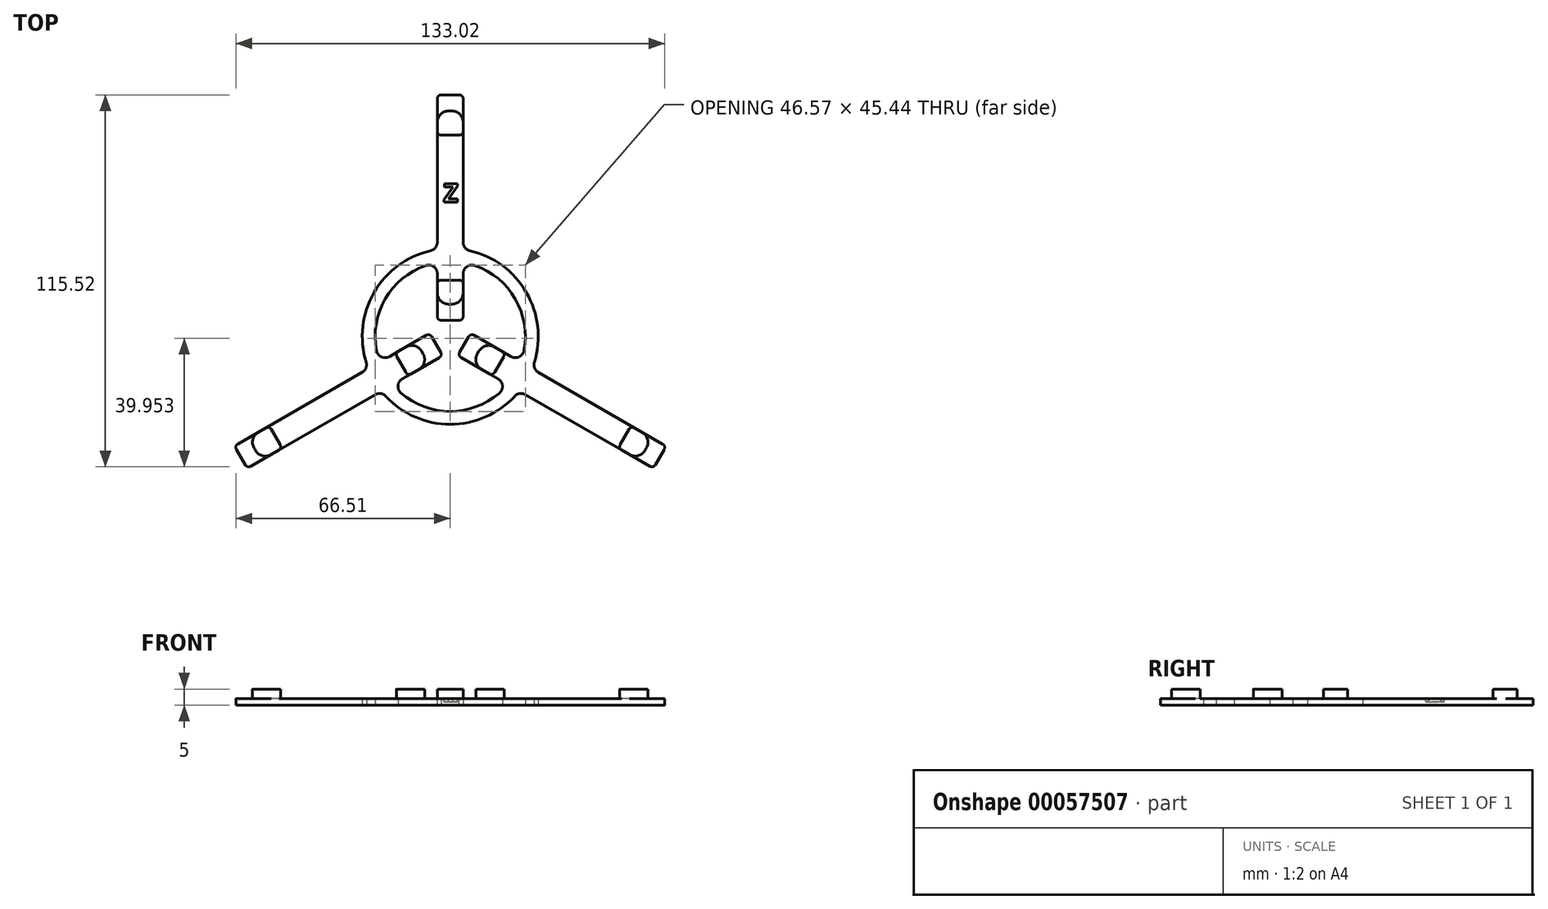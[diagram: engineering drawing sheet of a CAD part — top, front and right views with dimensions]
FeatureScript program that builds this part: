
annotation { "Feature Type Name" : "Feature", "Feature Type Description" : "" }
export const myFeature = defineFeature(function(context is Context, id is Id, definition is map)
    precondition{}
    {
        {
            var Q0;
            Q0=qCreatedBy(makeId("Top.planeOp"),FACE);
            var sketch = newSketch(context, id + "F0", { "sketchPlane" : qUnion([Q0])});
            skLineSegment(sketch, "E0", {"start": v(0, 0) * mm, "end": v(0, 85) * mm, "construction": true});
            skLineSegment(sketch, "E1", {"start": v(0, 0) * mm, "end": v(-73.61, -42.5) * mm, "construction": true});
            skLineSegment(sketch, "E2", {"start": v(0, 0) * mm, "end": v(73.61, -42.5) * mm, "construction": true});
            skLineSegment(sketch, "E3.rect.bottom", {"start": v(4, 5) * mm, "end": v(-4, 5) * mm});
            skLineSegment(sketch, "E3.rect.top", {"start": v(4, 75) * mm, "end": v(-4, 75) * mm});
            skLineSegment(sketch, "E3.rect.left", {"start": v(4, 5) * mm, "end": v(4, 75) * mm});
            skLineSegment(sketch, "E3.rect.right", {"start": v(-4, 5) * mm, "end": v(-4, 75) * mm});
            skPoint(sketch, "E3.rect.middle", {"position": v(0, 40) * mm});
            skLineSegment(sketch, "E4.rect.bottom", {"start": v(4, 10) * mm, "end": v(-4, 10) * mm});
            skLineSegment(sketch, "E4.rect.top", {"start": v(4, 17.5) * mm, "end": v(-4, 17.5) * mm});
            skLineSegment(sketch, "E4.rect.left", {"start": v(4, 10) * mm, "end": v(4, 17.5) * mm, "construction": true});
            skLineSegment(sketch, "E4.rect.right", {"start": v(-4, 10) * mm, "end": v(-4, 17.5) * mm, "construction": true});
            skPoint(sketch, "E4.rect.middle", {"position": v(0, 13.75) * mm});
            skLineSegment(sketch, "E5.rect.bottom", {"start": v(4, 70) * mm, "end": v(-4, 70) * mm});
            skLineSegment(sketch, "E5.rect.top", {"start": v(4, 62.5) * mm, "end": v(-4, 62.5) * mm});
            skLineSegment(sketch, "E5.rect.left", {"start": v(4, 70) * mm, "end": v(4, 62.5) * mm, "construction": true});
            skLineSegment(sketch, "E5.rect.right", {"start": v(-4, 70) * mm, "end": v(-4, 62.5) * mm, "construction": true});
            skPoint(sketch, "E5.rect.middle", {"position": v(0, 66.25) * mm});
            skPoint(sketch, "E6.1.0", {"position": v(-57.37, -33.12) * mm});
            skLineSegment(sketch, "E6.1.1", {"start": v(-6.33, 0.96) * mm, "end": v(-66.95, -34.04) * mm});
            skLineSegment(sketch, "E6.1.2", {"start": v(-2.33, -5.96) * mm, "end": v(-62.95, -40.96) * mm});
            skPoint(sketch, "E6.1.3", {"position": v(-11.9, -6.88) * mm});
            skPoint(sketch, "E6.1.4", {"position": v(-34.64, -20) * mm});
            skLineSegment(sketch, "E6.1.5", {"start": v(-58.62, -38.46) * mm, "end": v(-52.13, -34.71) * mm, "construction": true});
            skLineSegment(sketch, "E6.1.6", {"start": v(-6.33, 0.96) * mm, "end": v(-2.33, -5.96) * mm});
            skLineSegment(sketch, "E6.1.7", {"start": v(-66.95, -34.04) * mm, "end": v(-62.95, -40.96) * mm});
            skLineSegment(sketch, "E6.1.8", {"start": v(-62.62, -31.54) * mm, "end": v(-56.13, -27.79) * mm, "construction": true});
            skLineSegment(sketch, "E6.1.9", {"start": v(-56.13, -27.79) * mm, "end": v(-52.13, -34.71) * mm});
            skLineSegment(sketch, "E6.1.10", {"start": v(-10.66, -1.54) * mm, "end": v(-6.66, -8.46) * mm});
            skLineSegment(sketch, "E6.1.11", {"start": v(-17.16, -5.29) * mm, "end": v(-13.16, -12.21) * mm});
            skLineSegment(sketch, "E6.1.12", {"start": v(-10.66, -1.54) * mm, "end": v(-17.16, -5.29) * mm, "construction": true});
            skLineSegment(sketch, "E6.1.13", {"start": v(-62.62, -31.54) * mm, "end": v(-58.62, -38.46) * mm});
            skLineSegment(sketch, "E6.1.14", {"start": v(-6.66, -8.46) * mm, "end": v(-13.16, -12.21) * mm, "construction": true});
            skPoint(sketch, "E6.2.0", {"position": v(57.37, -33.12) * mm});
            skLineSegment(sketch, "E6.2.1", {"start": v(2.33, -5.96) * mm, "end": v(62.95, -40.96) * mm});
            skLineSegment(sketch, "E6.2.2", {"start": v(6.33, 0.96) * mm, "end": v(66.95, -34.04) * mm});
            skPoint(sketch, "E6.2.3", {"position": v(11.9, -6.88) * mm});
            skPoint(sketch, "E6.2.4", {"position": v(34.64, -20) * mm});
            skLineSegment(sketch, "E6.2.5", {"start": v(62.62, -31.54) * mm, "end": v(56.13, -27.79) * mm, "construction": true});
            skLineSegment(sketch, "E6.2.6", {"start": v(2.33, -5.96) * mm, "end": v(6.33, 0.96) * mm});
            skLineSegment(sketch, "E6.2.7", {"start": v(62.95, -40.96) * mm, "end": v(66.95, -34.04) * mm});
            skLineSegment(sketch, "E6.2.8", {"start": v(58.62, -38.46) * mm, "end": v(52.13, -34.71) * mm, "construction": true});
            skLineSegment(sketch, "E6.2.9", {"start": v(52.13, -34.71) * mm, "end": v(56.13, -27.79) * mm});
            skLineSegment(sketch, "E6.2.10", {"start": v(6.66, -8.46) * mm, "end": v(10.66, -1.54) * mm});
            skLineSegment(sketch, "E6.2.11", {"start": v(13.16, -12.21) * mm, "end": v(17.16, -5.29) * mm});
            skLineSegment(sketch, "E6.2.12", {"start": v(6.66, -8.46) * mm, "end": v(13.16, -12.21) * mm, "construction": true});
            skLineSegment(sketch, "E6.2.13", {"start": v(58.62, -38.46) * mm, "end": v(62.62, -31.54) * mm});
            skLineSegment(sketch, "E6.2.14", {"start": v(10.66, -1.54) * mm, "end": v(17.16, -5.29) * mm, "construction": true});
            skPoint(sketch, "E6.center", {"position": v(0, 0) * mm});
            skCircle(sketch, "E7", {"center": v(0, 0) * mm, "radius": 27.28 * mm});
            skCircle(sketch, "E8", {"center": v(0, 0) * mm, "radius": 23.28 * mm});
            skSolve(sketch);
        }
        {
            var Q0;
            {var subQ0=sQuery(id+"F0.wireOp",EDGE,"E5.rect.top");Q0=makeQuery(id+"F0.imprint","IMPRINT",FACE,{"disambiguationData":[TD([[makeQuery(id+"F0.imprint","IMPRINT",EDGE,{"derivedFrom":subQ0}),1.0]])]});}
            var Q1;
            {var subQ0=sQuery(id+"F0.wireOp",EDGE,"E7");var subQ1=sQuery(id+"F0.wireOp",EDGE,"E3.rect.left");var subQ2=makeQuery(id+"F0.imprint","INTERSECT",VERTEX,{"derivedFrom":[subQ1,subQ0]});Q1=makeQuery(id+"F0.imprint","IMPRINT",FACE,{"disambiguationData":[TD([[makeQuery(id+"F0.imprint","IMPRINT",EDGE,{"disambiguationData":[TD([[subQ2,1.0]])],"derivedFrom":subQ1}),1.0]])]});}
            var Q2;
            {var subQ0=sQuery(id+"F0.wireOp",EDGE,"E4.rect.top");Q2=makeQuery(id+"F0.imprint","IMPRINT",FACE,{"disambiguationData":[TD([[makeQuery(id+"F0.imprint","IMPRINT",EDGE,{"derivedFrom":subQ0}),-1.0]])]});}
            var Q3;
            {var subQ0=sQuery(id+"F0.wireOp",EDGE,"E3.rect.bottom");Q3=makeQuery(id+"F0.imprint","IMPRINT",FACE,{"disambiguationData":[TD([[makeQuery(id+"F0.imprint","IMPRINT",EDGE,{"derivedFrom":subQ0}),-1.0]])]});}
            var Q4;
            {var subQ0=sQuery(id+"F0.wireOp",EDGE,"E7");var subQ1=sQuery(id+"F0.wireOp",EDGE,"E3.rect.left");var subQ2=makeQuery(id+"F0.imprint","INTERSECT",VERTEX,{"derivedFrom":[subQ1,subQ0]});Q4=makeQuery(id+"F0.imprint","IMPRINT",FACE,{"disambiguationData":[TD([[makeQuery(id+"F0.imprint","IMPRINT",EDGE,{"disambiguationData":[TD([[subQ2,1.0]])],"derivedFrom":subQ1}),-1.0]])]});}
            var Q5;
            {var subQ0=sQuery(id+"F0.wireOp",EDGE,"E7");var subQ1=sQuery(id+"F0.wireOp",EDGE,"E3.rect.right");var subQ2=makeQuery(id+"F0.imprint","INTERSECT",VERTEX,{"derivedFrom":[subQ1,subQ0]});Q5=makeQuery(id+"F0.imprint","IMPRINT",FACE,{"disambiguationData":[TD([[makeQuery(id+"F0.imprint","IMPRINT",EDGE,{"disambiguationData":[TD([[subQ2,1.0]])],"derivedFrom":subQ1}),1.0]])]});}
            var Q6;
            {var subQ0=sQuery(id+"F0.wireOp",EDGE,"E5.rect.bottom");Q6=makeQuery(id+"F0.imprint","IMPRINT",FACE,{"disambiguationData":[TD([[makeQuery(id+"F0.imprint","IMPRINT",EDGE,{"derivedFrom":subQ0}),1.0]])]});}
            var Q7;
            {var subQ0=sQuery(id+"F0.wireOp",EDGE,"E3.rect.top");Q7=makeQuery(id+"F0.imprint","IMPRINT",FACE,{"disambiguationData":[TD([[makeQuery(id+"F0.imprint","IMPRINT",EDGE,{"derivedFrom":subQ0}),1.0]])]});}
            var Q8;
            {var subQ0=sQuery(id+"F0.wireOp",EDGE,"E7");var subQ1=sQuery(id+"F0.wireOp",EDGE,"E6.1.1");var subQ2=makeQuery(id+"F0.imprint","INTERSECT",VERTEX,{"derivedFrom":[subQ1,subQ0]});Q8=makeQuery(id+"F0.imprint","IMPRINT",FACE,{"disambiguationData":[TD([[makeQuery(id+"F0.imprint","IMPRINT",EDGE,{"disambiguationData":[TD([[subQ2,1.0]])],"derivedFrom":subQ1}),1.0]])]});}
            var Q9;
            {var subQ0=sQuery(id+"F0.wireOp",EDGE,"E6.1.11");Q9=makeQuery(id+"F0.imprint","IMPRINT",FACE,{"disambiguationData":[TD([[makeQuery(id+"F0.imprint","IMPRINT",EDGE,{"derivedFrom":subQ0}),-1.0]])]});}
            var Q10;
            {var subQ0=sQuery(id+"F0.wireOp",EDGE,"E6.1.6");Q10=makeQuery(id+"F0.imprint","IMPRINT",FACE,{"disambiguationData":[TD([[makeQuery(id+"F0.imprint","IMPRINT",EDGE,{"derivedFrom":subQ0}),-1.0]])]});}
            var Q11;
            {var subQ0=sQuery(id+"F0.wireOp",EDGE,"E6.1.9");Q11=makeQuery(id+"F0.imprint","IMPRINT",FACE,{"disambiguationData":[TD([[makeQuery(id+"F0.imprint","IMPRINT",EDGE,{"derivedFrom":subQ0}),1.0]])]});}
            var Q12;
            {var subQ0=sQuery(id+"F0.wireOp",EDGE,"E6.1.7");Q12=makeQuery(id+"F0.imprint","IMPRINT",FACE,{"disambiguationData":[TD([[makeQuery(id+"F0.imprint","IMPRINT",EDGE,{"derivedFrom":subQ0}),1.0]])]});}
            var Q13;
            {var subQ0=sQuery(id+"F0.wireOp",EDGE,"E6.2.6");Q13=makeQuery(id+"F0.imprint","IMPRINT",FACE,{"disambiguationData":[TD([[makeQuery(id+"F0.imprint","IMPRINT",EDGE,{"derivedFrom":subQ0}),-1.0]])]});}
            var Q14;
            {var subQ0=sQuery(id+"F0.wireOp",EDGE,"E6.2.11");Q14=makeQuery(id+"F0.imprint","IMPRINT",FACE,{"disambiguationData":[TD([[makeQuery(id+"F0.imprint","IMPRINT",EDGE,{"derivedFrom":subQ0}),-1.0]])]});}
            var Q15;
            {var subQ0=sQuery(id+"F0.wireOp",EDGE,"E7");var subQ1=sQuery(id+"F0.wireOp",EDGE,"E6.2.1");var subQ2=makeQuery(id+"F0.imprint","INTERSECT",VERTEX,{"derivedFrom":[subQ1,subQ0]});Q15=makeQuery(id+"F0.imprint","IMPRINT",FACE,{"disambiguationData":[TD([[makeQuery(id+"F0.imprint","IMPRINT",EDGE,{"disambiguationData":[TD([[subQ2,1.0]])],"derivedFrom":subQ1}),1.0]])]});}
            var Q16;
            {var subQ0=sQuery(id+"F0.wireOp",EDGE,"E6.2.9");Q16=makeQuery(id+"F0.imprint","IMPRINT",FACE,{"disambiguationData":[TD([[makeQuery(id+"F0.imprint","IMPRINT",EDGE,{"derivedFrom":subQ0}),1.0]])]});}
            var Q17;
            {var subQ0=sQuery(id+"F0.wireOp",EDGE,"E6.2.7");Q17=makeQuery(id+"F0.imprint","IMPRINT",FACE,{"disambiguationData":[TD([[makeQuery(id+"F0.imprint","IMPRINT",EDGE,{"derivedFrom":subQ0}),1.0]])]});}
            var Q18;
            {var subQ0=sQuery(id+"F0.wireOp",EDGE,"E7");var subQ1=sQuery(id+"F0.wireOp",EDGE,"E6.1.2");var subQ2=makeQuery(id+"F0.imprint","INTERSECT",VERTEX,{"derivedFrom":[subQ1,subQ0]});Q18=makeQuery(id+"F0.imprint","IMPRINT",FACE,{"disambiguationData":[TD([[makeQuery(id+"F0.imprint","IMPRINT",EDGE,{"disambiguationData":[TD([[subQ2,1.0]])],"derivedFrom":subQ1}),1.0]])]});}
            var Q19;
            {var subQ0=sQuery(id+"F0.wireOp",EDGE,"E6.2.9");Q19=makeQuery(id+"F0.imprint","IMPRINT",FACE,{"disambiguationData":[TD([[makeQuery(id+"F0.imprint","IMPRINT",EDGE,{"derivedFrom":subQ0}),-1.0]])]});}
            var Q20;
            {var subQ0=sQuery(id+"F0.wireOp",EDGE,"E6.2.10");Q20=makeQuery(id+"F0.imprint","IMPRINT",FACE,{"disambiguationData":[TD([[makeQuery(id+"F0.imprint","IMPRINT",EDGE,{"derivedFrom":subQ0}),-1.0]])]});}
            var Q21;
            {var subQ0=sQuery(id+"F0.wireOp",EDGE,"E6.1.10");Q21=makeQuery(id+"F0.imprint","IMPRINT",FACE,{"disambiguationData":[TD([[makeQuery(id+"F0.imprint","IMPRINT",EDGE,{"derivedFrom":subQ0}),-1.0]])]});}
            var Q22;
            {var subQ0=sQuery(id+"F0.wireOp",EDGE,"E4.rect.bottom");Q22=makeQuery(id+"F0.imprint","IMPRINT",FACE,{"disambiguationData":[TD([[makeQuery(id+"F0.imprint","IMPRINT",EDGE,{"derivedFrom":subQ0}),-1.0]])]});}
            var Q23;
            {var subQ0=sQuery(id+"F0.wireOp",EDGE,"E6.1.9");Q23=makeQuery(id+"F0.imprint","IMPRINT",FACE,{"disambiguationData":[TD([[makeQuery(id+"F0.imprint","IMPRINT",EDGE,{"derivedFrom":subQ0}),-1.0]])]});}
            extrude(context, id + "F1", {"entities" : qUnion([Q0, Q1, Q2, Q3, Q4, Q5, Q6, Q7, Q8, Q9, Q10, Q11, Q12, Q13, Q14, Q15, Q16, Q17, Q18, Q19, Q20, Q21, Q22, Q23]), "depth" : 2 * mm});
        }
        {
            var Q0;
            {var subQ0=sQuery(id+"F0.wireOp",EDGE,"E6.1.10");Q0=makeQuery(id+"F0.imprint","IMPRINT",FACE,{"disambiguationData":[TD([[makeQuery(id+"F0.imprint","IMPRINT",EDGE,{"derivedFrom":subQ0}),-1.0]])]});}
            var Q1;
            {var subQ0=sQuery(id+"F0.wireOp",EDGE,"E6.1.9");Q1=makeQuery(id+"F0.imprint","IMPRINT",FACE,{"disambiguationData":[TD([[makeQuery(id+"F0.imprint","IMPRINT",EDGE,{"derivedFrom":subQ0}),-1.0]])]});}
            var Q2;
            {var subQ0=sQuery(id+"F0.wireOp",EDGE,"E4.rect.bottom");Q2=makeQuery(id+"F0.imprint","IMPRINT",FACE,{"disambiguationData":[TD([[makeQuery(id+"F0.imprint","IMPRINT",EDGE,{"derivedFrom":subQ0}),-1.0]])]});}
            var Q3;
            {var subQ0=sQuery(id+"F0.wireOp",EDGE,"E6.2.10");Q3=makeQuery(id+"F0.imprint","IMPRINT",FACE,{"disambiguationData":[TD([[makeQuery(id+"F0.imprint","IMPRINT",EDGE,{"derivedFrom":subQ0}),-1.0]])]});}
            var Q4;
            {var subQ0=sQuery(id+"F0.wireOp",EDGE,"E6.2.9");Q4=makeQuery(id+"F0.imprint","IMPRINT",FACE,{"disambiguationData":[TD([[makeQuery(id+"F0.imprint","IMPRINT",EDGE,{"derivedFrom":subQ0}),-1.0]])]});}
            var Q5;
            {var subQ0=sQuery(id+"F0.wireOp",EDGE,"E5.rect.bottom");Q5=makeQuery(id+"F0.imprint","IMPRINT",FACE,{"disambiguationData":[TD([[makeQuery(id+"F0.imprint","IMPRINT",EDGE,{"derivedFrom":subQ0}),1.0]])]});}
            extrude(context, id + "F2", {"entities" : qUnion([Q0, Q1, Q2, Q3, Q4, Q5]), "operationType" : NewBodyOperationType.ADD, "depth" : 5 * mm});
        }
        {
            var Q0;
            Q0=makeQuery(id+"F2.opExtrude","SWEPT_EDGE",EDGE,{"disambiguationData":[OSD([sQuery(id+"F0.wireOp",EDGE,"E6.1.1"),sQuery(id+"F0.wireOp",EDGE,"E6.1.13")])]});
            var Q1;
            Q1=makeQuery(id+"F2.opExtrude","SWEPT_EDGE",EDGE,{"disambiguationData":[OSD([sQuery(id+"F0.wireOp",EDGE,"E6.1.2"),sQuery(id+"F0.wireOp",EDGE,"E6.1.13")])]});
            var Q2;
            Q2=makeQuery(id+"F2.opExtrude","SWEPT_EDGE",EDGE,{"disambiguationData":[OSD([sQuery(id+"F0.wireOp",EDGE,"E6.1.2"),sQuery(id+"F0.wireOp",EDGE,"E6.1.10")])]});
            var Q3;
            Q3=makeQuery(id+"F2.opExtrude","SWEPT_EDGE",EDGE,{"disambiguationData":[OSD([sQuery(id+"F0.wireOp",EDGE,"E6.1.1"),sQuery(id+"F0.wireOp",EDGE,"E6.1.10")])]});
            var Q4;
            Q4=makeQuery(id+"F2.opExtrude","SWEPT_EDGE",EDGE,{"disambiguationData":[OSD([sQuery(id+"F0.wireOp",EDGE,"E3.rect.left"),sQuery(id+"F0.wireOp",EDGE,"E4.rect.bottom")])]});
            var Q5;
            Q5=makeQuery(id+"F2.opExtrude","SWEPT_EDGE",EDGE,{"disambiguationData":[OSD([sQuery(id+"F0.wireOp",EDGE,"E3.rect.right"),sQuery(id+"F0.wireOp",EDGE,"E4.rect.bottom")])]});
            var Q6;
            Q6=makeQuery(id+"F2.opExtrude","SWEPT_EDGE",EDGE,{"disambiguationData":[OSD([sQuery(id+"F0.wireOp",EDGE,"E6.2.2"),sQuery(id+"F0.wireOp",EDGE,"E6.2.10")])]});
            var Q7;
            Q7=makeQuery(id+"F2.opExtrude","SWEPT_EDGE",EDGE,{"disambiguationData":[OSD([sQuery(id+"F0.wireOp",EDGE,"E6.2.1"),sQuery(id+"F0.wireOp",EDGE,"E6.2.10")])]});
            var Q8;
            Q8=makeQuery(id+"F2.opExtrude","SWEPT_EDGE",EDGE,{"disambiguationData":[OSD([sQuery(id+"F0.wireOp",EDGE,"E3.rect.left"),sQuery(id+"F0.wireOp",EDGE,"E5.rect.bottom")])]});
            var Q9;
            Q9=makeQuery(id+"F2.opExtrude","SWEPT_EDGE",EDGE,{"disambiguationData":[OSD([sQuery(id+"F0.wireOp",EDGE,"E3.rect.right"),sQuery(id+"F0.wireOp",EDGE,"E5.rect.bottom")])]});
            var Q10;
            Q10=makeQuery(id+"F2.opExtrude","SWEPT_EDGE",EDGE,{"disambiguationData":[OSD([sQuery(id+"F0.wireOp",EDGE,"E6.2.1"),sQuery(id+"F0.wireOp",EDGE,"E6.2.13")])]});
            var Q11;
            Q11=makeQuery(id+"F2.opExtrude","SWEPT_EDGE",EDGE,{"disambiguationData":[OSD([sQuery(id+"F0.wireOp",EDGE,"E6.2.2"),sQuery(id+"F0.wireOp",EDGE,"E6.2.13")])]});
            fillet(context, id + "F3", {"entities" : qUnion([Q0, Q1, Q2, Q3, Q4, Q5, Q6, Q7, Q8, Q9, Q10, Q11]), "radius" : 3.5 * mm, "tangentPropagation" : true, "allowEdgeOverflow" : false});
        }
        {
            var Q0;
            {var subQ1=sQuery(id+"F0.wireOp",EDGE,"E3.rect.right");var subQ6=sQuery(id+"F0.wireOp",EDGE,"E4.rect.top");var subQ8=sQuery(id+"F0.wireOp",EDGE,"E8");var subQ13=sQuery(id+"F0.wireOp",EDGE,"E3.rect.bottom");var subQ14=sQuery(id+"F0.wireOp",EDGE,"E3.rect.left");var subQ19=sQuery(id+"F0.wireOp",EDGE,"E6.1.2");var subQ25=sQuery(id+"F0.wireOp",EDGE,"E6.1.6");var subQ27=sQuery(id+"F0.wireOp",EDGE,"E6.2.2");var subQ29=sQuery(id+"F0.wireOp",EDGE,"E7");var subQ31=sQuery(id+"F0.wireOp",EDGE,"E6.1.1");var subQ33=sQuery(id+"F0.wireOp",EDGE,"E3.rect.top");var subQ42=sQuery(id+"F0.wireOp",EDGE,"E6.1.7");var subQ49=sQuery(id+"F0.wireOp",EDGE,"E6.2.1");var subQ58=sQuery(id+"F0.wireOp",EDGE,"E6.2.6");var subQ67=sQuery(id+"F0.wireOp",EDGE,"E6.2.7");Q0=makeQuery(id+"F2.boolean.opBoolean","SPLIT",FACE,{"disambiguationData":[TD([makeQuery(id+"F2.opExtrude","SWEPT_FACE",FACE,{"disambiguationData":[OSD([subQ6])]})])],"derivedFrom":makeQuery(id+"F1.opExtrude","CAP_FACE",FACE,{"disambiguationData":[OSD([subQ13,subQ33,subQ14,subQ1,subQ31,subQ19,subQ25,subQ42,subQ49,subQ27,subQ58,subQ67,subQ29,subQ8])],"isStart":false})});}
            var sketch = newSketch(context, id + "F4", { "sketchPlane" : qUnion([Q0])});
            skText(sketch, "E9", { "text": "Z", "fontName": "OpenSans-Bold.ttf"});
            const initialGuessF4  = {"E9": [-0.0021, 0.04172, 1, 0, 0.00571]};
            skSetInitialGuess(sketch, initialGuessF4);
            skSolve(sketch);
        }
        {
            var Q0;
            Q0=makeQuery(id+"F4.imprint","IMPRINT",FACE,{"disambiguationData":[TD([[makeQuery(id+"F4.imprint","IMPRINT",EDGE,{"derivedFrom":sQuery(id+"F4.wireOp",EDGE,"E9.sketch_text.stroke-0")}),-1.0]])]});
            extrude(context, id + "F5", {"entities" : qUnion([Q0]), "operationType" : NewBodyOperationType.REMOVE, "oppositeDirection" : true, "depth" : 1 * mm});
        }
        {
            var Q0;
            Q0=makeQuery(id+"F1.opExtrude","SWEPT_EDGE",EDGE,{"disambiguationData":[OSD([sQuery(id+"F0.wireOp",EDGE,"E3.rect.right"),sQuery(id+"F0.wireOp",EDGE,"E8")])]});
            var Q1;
            Q1=makeQuery(id+"F1.opExtrude","SWEPT_EDGE",EDGE,{"disambiguationData":[OSD([sQuery(id+"F0.wireOp",EDGE,"E6.1.2"),sQuery(id+"F0.wireOp",EDGE,"E7")])]});
            var Q2;
            Q2=makeQuery(id+"F1.opExtrude","SWEPT_EDGE",EDGE,{"disambiguationData":[OSD([sQuery(id+"F0.wireOp",EDGE,"E6.2.1"),sQuery(id+"F0.wireOp",EDGE,"E7")])]});
            var Q3;
            Q3=makeQuery(id+"F1.opExtrude","SWEPT_EDGE",EDGE,{"disambiguationData":[OSD([sQuery(id+"F0.wireOp",EDGE,"E6.2.2"),sQuery(id+"F0.wireOp",EDGE,"E7")])]});
            var Q4;
            Q4=makeQuery(id+"F1.opExtrude","SWEPT_EDGE",EDGE,{"disambiguationData":[OSD([sQuery(id+"F0.wireOp",EDGE,"E3.rect.left"),sQuery(id+"F0.wireOp",EDGE,"E7")])]});
            var Q5;
            Q5=makeQuery(id+"F1.opExtrude","SWEPT_EDGE",EDGE,{"disambiguationData":[OSD([sQuery(id+"F0.wireOp",EDGE,"E3.rect.left"),sQuery(id+"F0.wireOp",EDGE,"E8")])]});
            var Q6;
            Q6=makeQuery(id+"F1.opExtrude","SWEPT_EDGE",EDGE,{"disambiguationData":[OSD([sQuery(id+"F0.wireOp",EDGE,"E6.1.2"),sQuery(id+"F0.wireOp",EDGE,"E8")])]});
            var Q7;
            Q7=makeQuery(id+"F1.opExtrude","SWEPT_EDGE",EDGE,{"disambiguationData":[OSD([sQuery(id+"F0.wireOp",EDGE,"E3.rect.right"),sQuery(id+"F0.wireOp",EDGE,"E7")])]});
            var Q8;
            Q8=makeQuery(id+"F1.opExtrude","SWEPT_EDGE",EDGE,{"disambiguationData":[OSD([sQuery(id+"F0.wireOp",EDGE,"E6.1.1"),sQuery(id+"F0.wireOp",EDGE,"E7")])]});
            var Q9;
            Q9=makeQuery(id+"F1.opExtrude","SWEPT_EDGE",EDGE,{"disambiguationData":[OSD([sQuery(id+"F0.wireOp",EDGE,"E6.1.1"),sQuery(id+"F0.wireOp",EDGE,"E8")])]});
            var Q10;
            Q10=makeQuery(id+"F1.opExtrude","SWEPT_EDGE",EDGE,{"disambiguationData":[OSD([sQuery(id+"F0.wireOp",EDGE,"E6.2.1"),sQuery(id+"F0.wireOp",EDGE,"E8")])]});
            var Q11;
            Q11=makeQuery(id+"F1.opExtrude","SWEPT_EDGE",EDGE,{"disambiguationData":[OSD([sQuery(id+"F0.wireOp",EDGE,"E6.2.2"),sQuery(id+"F0.wireOp",EDGE,"E8")])]});
            fillet(context, id + "F6", {"entities" : qUnion([Q0, Q1, Q2, Q3, Q4, Q5, Q6, Q7, Q8, Q9, Q10, Q11]), "radius" : 2.7 * mm, "tangentPropagation" : true, "allowEdgeOverflow" : false});
        }
        {
            var Q0;
            Q0=makeQuery(id+"F1.opExtrude","SWEPT_EDGE",EDGE,{"disambiguationData":[OSD([sQuery(id+"F0.wireOp",EDGE,"E6.1.2"),sQuery(id+"F0.wireOp",EDGE,"E6.1.7")])]});
            var Q1;
            Q1=makeQuery(id+"F1.opExtrude","SWEPT_EDGE",EDGE,{"disambiguationData":[OSD([sQuery(id+"F0.wireOp",EDGE,"E6.1.1"),sQuery(id+"F0.wireOp",EDGE,"E6.1.7")])]});
            var Q2;
            Q2=makeQuery(id+"F1.opExtrude","SWEPT_EDGE",EDGE,{"disambiguationData":[OSD([sQuery(id+"F0.wireOp",EDGE,"E6.2.1"),sQuery(id+"F0.wireOp",EDGE,"E6.2.7")])]});
            var Q3;
            Q3=makeQuery(id+"F1.opExtrude","SWEPT_EDGE",EDGE,{"disambiguationData":[OSD([sQuery(id+"F0.wireOp",EDGE,"E6.2.2"),sQuery(id+"F0.wireOp",EDGE,"E6.2.7")])]});
            var Q4;
            Q4=makeQuery(id+"F1.opExtrude","SWEPT_EDGE",EDGE,{"disambiguationData":[OSD([sQuery(id+"F0.wireOp",EDGE,"E3.rect.top"),sQuery(id+"F0.wireOp",EDGE,"E3.rect.right")])]});
            var Q5;
            Q5=makeQuery(id+"F1.opExtrude","SWEPT_EDGE",EDGE,{"disambiguationData":[OSD([sQuery(id+"F0.wireOp",EDGE,"E3.rect.top"),sQuery(id+"F0.wireOp",EDGE,"E3.rect.left")])]});
            var Q6;
            Q6=makeQuery(id+"F1.opExtrude","SWEPT_EDGE",EDGE,{"disambiguationData":[OSD([sQuery(id+"F0.wireOp",EDGE,"E6.2.1"),sQuery(id+"F0.wireOp",EDGE,"E6.2.6")])]});
            var Q7;
            Q7=makeQuery(id+"F1.opExtrude","SWEPT_EDGE",EDGE,{"disambiguationData":[OSD([sQuery(id+"F0.wireOp",EDGE,"E6.2.2"),sQuery(id+"F0.wireOp",EDGE,"E6.2.6")])]});
            var Q8;
            Q8=makeQuery(id+"F1.opExtrude","SWEPT_EDGE",EDGE,{"disambiguationData":[OSD([sQuery(id+"F0.wireOp",EDGE,"E3.rect.bottom"),sQuery(id+"F0.wireOp",EDGE,"E3.rect.right")])]});
            var Q9;
            Q9=makeQuery(id+"F1.opExtrude","SWEPT_EDGE",EDGE,{"disambiguationData":[OSD([sQuery(id+"F0.wireOp",EDGE,"E3.rect.bottom"),sQuery(id+"F0.wireOp",EDGE,"E3.rect.left")])]});
            var Q10;
            Q10=makeQuery(id+"F1.opExtrude","SWEPT_EDGE",EDGE,{"disambiguationData":[OSD([sQuery(id+"F0.wireOp",EDGE,"E6.1.2"),sQuery(id+"F0.wireOp",EDGE,"E6.1.6")])]});
            var Q11;
            Q11=makeQuery(id+"F1.opExtrude","SWEPT_EDGE",EDGE,{"disambiguationData":[OSD([sQuery(id+"F0.wireOp",EDGE,"E6.1.1"),sQuery(id+"F0.wireOp",EDGE,"E6.1.6")])]});
            var Q12;
            Q12=makeQuery(id+"F2.opExtrude","SWEPT_EDGE",EDGE,{"disambiguationData":[OSD([sQuery(id+"F0.wireOp",EDGE,"E6.1.2"),sQuery(id+"F0.wireOp",EDGE,"E6.1.9")])]});
            var Q13;
            Q13=makeQuery(id+"F2.opExtrude","SWEPT_EDGE",EDGE,{"disambiguationData":[OSD([sQuery(id+"F0.wireOp",EDGE,"E6.1.1"),sQuery(id+"F0.wireOp",EDGE,"E6.1.9")])]});
            var Q14;
            Q14=makeQuery(id+"F2.opExtrude","SWEPT_EDGE",EDGE,{"disambiguationData":[OSD([sQuery(id+"F0.wireOp",EDGE,"E6.2.1"),sQuery(id+"F0.wireOp",EDGE,"E6.2.11")])]});
            var Q15;
            Q15=makeQuery(id+"F2.opExtrude","SWEPT_EDGE",EDGE,{"disambiguationData":[OSD([sQuery(id+"F0.wireOp",EDGE,"E3.rect.left"),sQuery(id+"F0.wireOp",EDGE,"E4.rect.top")])]});
            var Q16;
            Q16=makeQuery(id+"F2.opExtrude","SWEPT_EDGE",EDGE,{"disambiguationData":[OSD([sQuery(id+"F0.wireOp",EDGE,"E3.rect.right"),sQuery(id+"F0.wireOp",EDGE,"E4.rect.top")])]});
            var Q17;
            Q17=makeQuery(id+"F2.opExtrude","SWEPT_EDGE",EDGE,{"disambiguationData":[OSD([sQuery(id+"F0.wireOp",EDGE,"E6.2.2"),sQuery(id+"F0.wireOp",EDGE,"E6.2.11")])]});
            var Q18;
            Q18=makeQuery(id+"F2.opExtrude","SWEPT_EDGE",EDGE,{"disambiguationData":[OSD([sQuery(id+"F0.wireOp",EDGE,"E6.2.2"),sQuery(id+"F0.wireOp",EDGE,"E6.2.9")])]});
            var Q19;
            Q19=makeQuery(id+"F2.opExtrude","SWEPT_EDGE",EDGE,{"disambiguationData":[OSD([sQuery(id+"F0.wireOp",EDGE,"E6.2.1"),sQuery(id+"F0.wireOp",EDGE,"E6.2.9")])]});
            var Q20;
            Q20=makeQuery(id+"F2.opExtrude","SWEPT_EDGE",EDGE,{"disambiguationData":[OSD([sQuery(id+"F0.wireOp",EDGE,"E3.rect.left"),sQuery(id+"F0.wireOp",EDGE,"E5.rect.top")])]});
            var Q21;
            Q21=makeQuery(id+"F2.opExtrude","SWEPT_EDGE",EDGE,{"disambiguationData":[OSD([sQuery(id+"F0.wireOp",EDGE,"E3.rect.right"),sQuery(id+"F0.wireOp",EDGE,"E5.rect.top")])]});
            var Q22;
            Q22=makeQuery(id+"F2.opExtrude","SWEPT_EDGE",EDGE,{"disambiguationData":[OSD([sQuery(id+"F0.wireOp",EDGE,"E6.1.2"),sQuery(id+"F0.wireOp",EDGE,"E6.1.11")])]});
            var Q23;
            Q23=makeQuery(id+"F2.opExtrude","SWEPT_EDGE",EDGE,{"disambiguationData":[OSD([sQuery(id+"F0.wireOp",EDGE,"E6.1.1"),sQuery(id+"F0.wireOp",EDGE,"E6.1.11")])]});
            fillet(context, id + "F7", {"entities" : qUnion([Q0, Q1, Q2, Q3, Q4, Q5, Q6, Q7, Q8, Q9, Q10, Q11, Q12, Q13, Q14, Q15, Q16, Q17, Q18, Q19, Q20, Q21, Q22, Q23]), "radius" : 1.2 * mm, "tangentPropagation" : true, "allowEdgeOverflow" : false});
        }
    });
